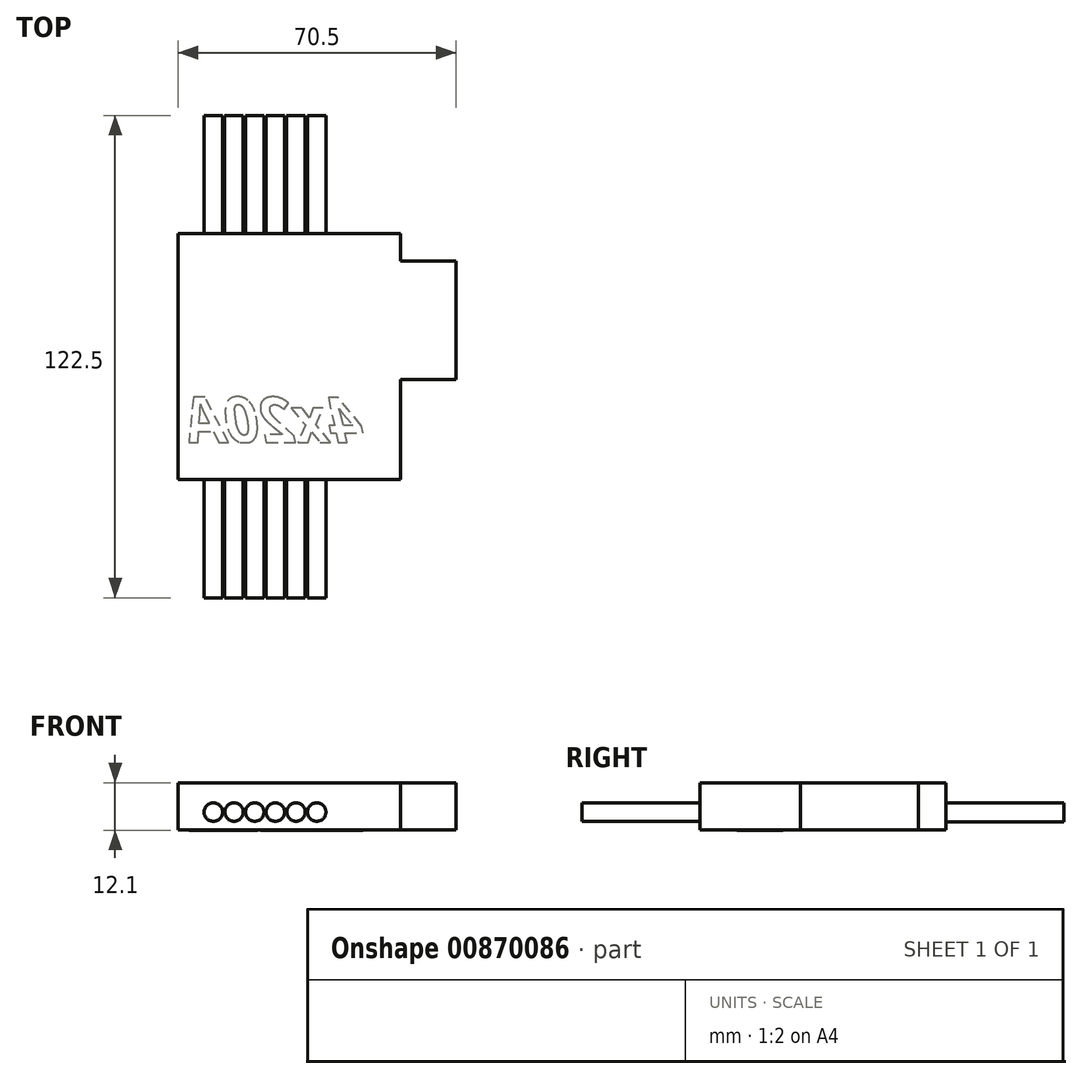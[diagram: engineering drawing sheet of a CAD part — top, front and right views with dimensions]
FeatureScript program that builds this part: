
annotation { "Feature Type Name" : "Feature", "Feature Type Description" : "" }
export const myFeature = defineFeature(function(context is Context, id is Id, definition is map)
    precondition{}
    {
        {
            var Q0;
            Q0=qCreatedBy(makeId("Top.planeOp"),FACE);
            var sketch = newSketch(context, id + "F0", { "sketchPlane" : qUnion([Q0])});
            skLineSegment(sketch, "E0.bottom", {"start": v(28.25, 31.25) * mm, "end": v(-28.25, 31.25) * mm});
            skLineSegment(sketch, "E0.top", {"start": v(28.25, -31.25) * mm, "end": v(-28.25, -31.25) * mm});
            skLineSegment(sketch, "E0.left", {"start": v(28.25, 31.25) * mm, "end": v(28.25, -31.25) * mm});
            skLineSegment(sketch, "E0.right", {"start": v(-28.25, 31.25) * mm, "end": v(-28.25, -31.25) * mm});
            skPoint(sketch, "E0.middle", {"position": v(0, 0) * mm});
            skSolve(sketch);
        }
        {
            var Q0;
            Q0 = qSketchRegion(id + "F0", true);
            extrude(context, id + "F1", {"entities" : qUnion([Q0]), "depth" : 12 * mm, "offsetDistance" : 25 * mm});
        }
        {
            var Q0;
            Q0=makeQuery(id+"F1.opExtrude","SWEPT_FACE",FACE,{"disambiguationData":[OSD([sQuery(id+"F0.wireOp",EDGE,"E0.top")])]});
            var sketch = newSketch(context, id + "F2", { "sketchPlane" : qUnion([Q0])});
            skCircle(sketch, "E1", {"center": v(-19.33, 4.55) * mm, "radius": 2.35 * mm});
            skCircle(sketch, "E2.1.0.0", {"center": v(-14.08, 4.55) * mm, "radius": 2.35 * mm});
            skCircle(sketch, "E2.2.0.0", {"center": v(-8.83, 4.55) * mm, "radius": 2.35 * mm});
            skCircle(sketch, "E2.3.0.0", {"center": v(-3.58, 4.55) * mm, "radius": 2.35 * mm});
            skCircle(sketch, "E2.4.0.0", {"center": v(1.67, 4.55) * mm, "radius": 2.35 * mm});
            skCircle(sketch, "E2.5.0.0", {"center": v(6.92, 4.55) * mm, "radius": 2.35 * mm});
            skLineSegment(sketch, "E2.direction1", {"start": v(-19.33, 4.55) * mm, "end": v(-14.08, 4.55) * mm, "construction": true});
            skSolve(sketch);
        }
        {
            var Q0;
            Q0=makeQuery(id+"F2.imprint","IMPRINT",FACE,{"disambiguationData":[TD([[makeQuery(id+"F2.imprint","IMPRINT",EDGE,{"derivedFrom":sQuery(id+"F2.wireOp",EDGE,"E1")}),1.0]])]});
            var Q1;
            Q1=makeQuery(id+"F2.imprint","IMPRINT",FACE,{"disambiguationData":[TD([[makeQuery(id+"F2.imprint","IMPRINT",EDGE,{"derivedFrom":sQuery(id+"F2.wireOp",EDGE,"E2.1.0.0")}),1.0]])]});
            var Q2;
            Q2=makeQuery(id+"F2.imprint","IMPRINT",FACE,{"disambiguationData":[TD([[makeQuery(id+"F2.imprint","IMPRINT",EDGE,{"derivedFrom":sQuery(id+"F2.wireOp",EDGE,"E2.2.0.0")}),1.0]])]});
            var Q3;
            Q3=makeQuery(id+"F2.imprint","IMPRINT",FACE,{"disambiguationData":[TD([[makeQuery(id+"F2.imprint","IMPRINT",EDGE,{"derivedFrom":sQuery(id+"F2.wireOp",EDGE,"E2.3.0.0")}),1.0]])]});
            var Q4;
            Q4=makeQuery(id+"F2.imprint","IMPRINT",FACE,{"disambiguationData":[TD([[makeQuery(id+"F2.imprint","IMPRINT",EDGE,{"derivedFrom":sQuery(id+"F2.wireOp",EDGE,"E2.4.0.0")}),1.0]])]});
            var Q5;
            Q5=makeQuery(id+"F2.imprint","IMPRINT",FACE,{"disambiguationData":[TD([[makeQuery(id+"F2.imprint","IMPRINT",EDGE,{"derivedFrom":sQuery(id+"F2.wireOp",EDGE,"E2.5.0.0")}),1.0]])]});
            extrude(context, id + "F3", {"entities" : qUnion([Q0, Q1, Q2, Q3, Q4, Q5]), "operationType" : NewBodyOperationType.ADD, "depth" : 30 * mm, "offsetDistance" : 25 * mm});
        }
        {
            var Q0;
            Q0=makeQuery(id+"F1.opExtrude","SWEPT_FACE",FACE,{"disambiguationData":[OSD([sQuery(id+"F0.wireOp",EDGE,"E0.bottom")])]});
            var sketch = newSketch(context, id + "F4", { "sketchPlane" : qUnion([Q0])});
            skCircle(sketch, "E3", {"center": v(-6.9, 4.46) * mm, "radius": 2.35 * mm});
            skCircle(sketch, "E4.1.0.0", {"center": v(-1.65, 4.46) * mm, "radius": 2.35 * mm});
            skCircle(sketch, "E4.2.0.0", {"center": v(3.6, 4.46) * mm, "radius": 2.35 * mm});
            skCircle(sketch, "E4.3.0.0", {"center": v(8.85, 4.46) * mm, "radius": 2.35 * mm});
            skCircle(sketch, "E4.4.0.0", {"center": v(14.1, 4.46) * mm, "radius": 2.35 * mm});
            skCircle(sketch, "E4.5.0.0", {"center": v(19.35, 4.46) * mm, "radius": 2.35 * mm});
            skLineSegment(sketch, "E4.direction1", {"start": v(-6.9, 4.46) * mm, "end": v(-1.65, 4.46) * mm, "construction": true});
            skLineSegment(sketch, "E5", {"start": v(-9.15, 0) * mm, "end": v(-9.15, 2) * mm});
            skLineSegment(sketch, "E6", {"start": v(28.25, 2.05) * mm, "end": v(21.75, 2.05) * mm});
            skSolve(sketch);
        }
        {
            var Q0;
            Q0 = qSketchRegion(id + "F4", true);
            extrude(context, id + "F5", {"entities" : qUnion([Q0]), "operationType" : NewBodyOperationType.ADD, "depth" : 30 * mm, "offsetDistance" : 25 * mm});
        }
        {
            var Q0;
            Q0=makeQuery(id+"F1.opExtrude","SWEPT_FACE",FACE,{"disambiguationData":[OSD([sQuery(id+"F0.wireOp",EDGE,"E0.left")])]});
            var sketch = newSketch(context, id + "F6", { "sketchPlane" : qUnion([Q0])});
            skLineSegment(sketch, "E7", {"start": v(31.25, 6) * mm, "end": v(24.25, 6) * mm});
            skLineSegment(sketch, "E8", {"start": v(24.25, 12) * mm, "end": v(24.25, 0) * mm});
            skLineSegment(sketch, "E9", {"start": v(24.25, 0) * mm, "end": v(-5.75, 0) * mm});
            skLineSegment(sketch, "E10", {"start": v(-5.75, 0) * mm, "end": v(-5.75, 12) * mm});
            skLineSegment(sketch, "E11", {"start": v(-5.75, 12) * mm, "end": v(24.25, 12) * mm});
            skSolve(sketch);
        }
        {
            var Q0;
            {var subQ0=sQuery(id+"F6.wireOp",EDGE,"E9");Q0=makeQuery(id+"F6.imprint","IMPRINT",FACE,{"disambiguationData":[TD([[makeQuery(id+"F6.imprint","IMPRINT",EDGE,{"derivedFrom":subQ0}),-1.0]])]});}
            extrude(context, id + "F7", {"entities" : qUnion([Q0]), "operationType" : NewBodyOperationType.ADD, "depth" : 14 * mm, "offsetDistance" : 25 * mm});
        }
        {
            var Q0;
            Q0=makeQuery(id+"F7.boolean.opBoolean","MERGE",FACE,{"derivedFrom":[makeQuery(id+"F1.opExtrude","CAP_FACE",FACE,{"disambiguationData":[OSD([sQuery(id+"F0.wireOp",EDGE,"E0.bottom"),sQuery(id+"F0.wireOp",EDGE,"E0.top"),sQuery(id+"F0.wireOp",EDGE,"E0.left"),sQuery(id+"F0.wireOp",EDGE,"E0.right")])],"isStart":true}),makeQuery(id+"F7.opExtrude","SWEPT_FACE",FACE,{"disambiguationData":[OSD([sQuery(id+"F6.wireOp",EDGE,"E9")])]})]});
            var sketch = newSketch(context, id + "F8", { "sketchPlane" : qUnion([Q0])});
            skLineSegment(sketch, "E12.bottom", {"start": v(-26.78, 23.7) * mm, "end": v(18.5, 23.7) * mm});
            skLineSegment(sketch, "E12.top", {"start": v(-26.78, 21.77) * mm, "end": v(18.5, 21.77) * mm});
            skLineSegment(sketch, "E12.left", {"start": v(-26.78, 23.7) * mm, "end": v(-26.78, 21.77) * mm});
            skLineSegment(sketch, "E12.right", {"start": v(18.5, 23.7) * mm, "end": v(18.5, 21.77) * mm});
            skText(sketch, "E13", { "text": "4x20A", "fontName": "OpenSans-BoldItalic.ttf"});
            const initialGuessF8  = {"E13": [0.0185, 0.02177, -1, 0, 0.01153]};
            skSetInitialGuess(sketch, initialGuessF8);
            skSolve(sketch);
        }
        {
            var Q0;
            Q0=makeQuery(id+"F8.imprint","IMPRINT",FACE,{"disambiguationData":[TD([[makeQuery(id+"F8.imprint","IMPRINT",EDGE,{"derivedFrom":sQuery(id+"F8.wireOp",EDGE,"E13.sketch_text.stroke-69")}),-1.0]])]});
            var Q1;
            {var subQ6=sQuery(id+"F8.wireOp",EDGE,"E13.sketch_text.stroke-51");Q1=makeQuery(id+"F8.imprint","IMPRINT",FACE,{"disambiguationData":[TD([[makeQuery(id+"F8.imprint","IMPRINT",EDGE,{"derivedFrom":subQ6}),-1.0]])]});}
            var Q2;
            {var subQ2=sQuery(id+"F8.wireOp",EDGE,"E13.sketch_text.stroke-31");Q2=makeQuery(id+"F8.imprint","IMPRINT",FACE,{"disambiguationData":[TD([[makeQuery(id+"F8.imprint","IMPRINT",EDGE,{"derivedFrom":subQ2}),-1.0]])]});}
            var Q3;
            Q3=makeQuery(id+"F8.imprint","IMPRINT",FACE,{"disambiguationData":[TD([[makeQuery(id+"F8.imprint","IMPRINT",EDGE,{"derivedFrom":sQuery(id+"F8.wireOp",EDGE,"E13.sketch_text.stroke-18")}),-1.0]])]});
            var Q4;
            Q4=makeQuery(id+"F8.imprint","IMPRINT",FACE,{"disambiguationData":[TD([[makeQuery(id+"F8.imprint","IMPRINT",EDGE,{"derivedFrom":sQuery(id+"F8.wireOp",EDGE,"E13.sketch_text.stroke-0")}),-1.0]])]});
            extrude(context, id + "F9", {"entities" : qUnion([Q0, Q1, Q2, Q3, Q4]), "operationType" : NewBodyOperationType.ADD, "depth" : .1 * mm, "offsetDistance" : 25 * mm});
        }
    });
